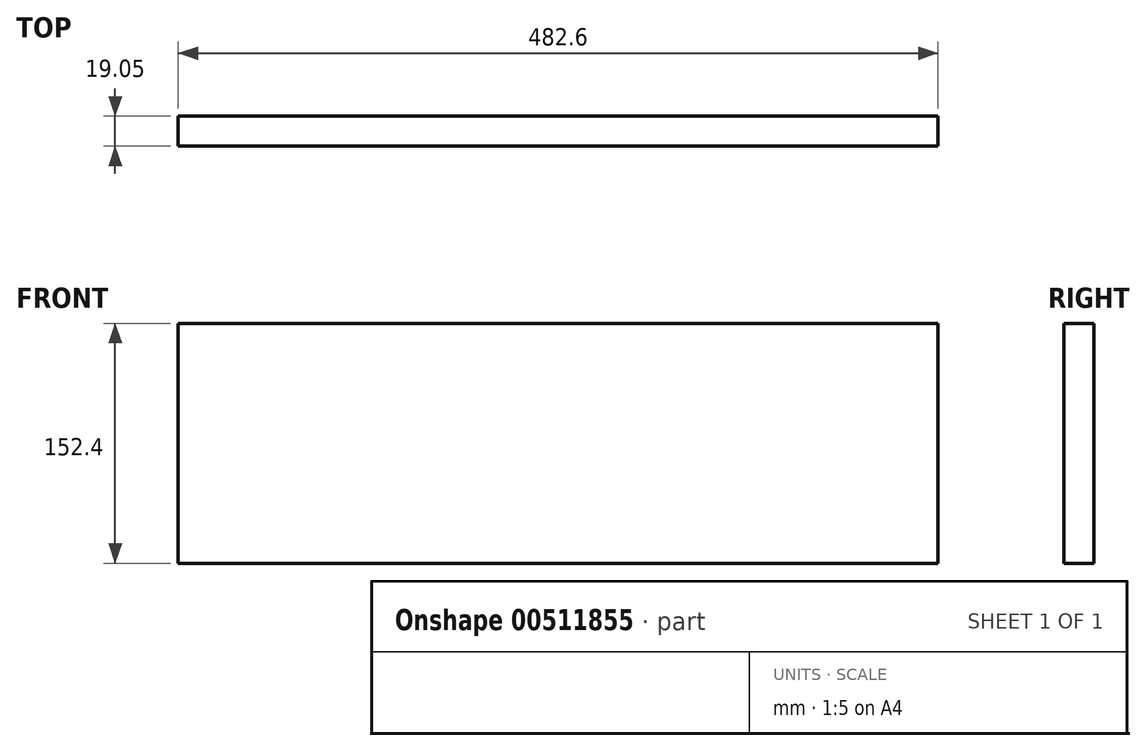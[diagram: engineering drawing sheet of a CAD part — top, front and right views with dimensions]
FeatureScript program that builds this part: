
annotation { "Feature Type Name" : "Feature", "Feature Type Description" : "" }
export const myFeature = defineFeature(function(context is Context, id is Id, definition is map)
    precondition{}
    {
        {
            var Q0;
            Q0=qCreatedBy(makeId("Front.planeOp"),FACE);
            var sketch = newSketch(context, id + "F0", { "sketchPlane" : qUnion([Q0])});
            skLineSegment(sketch, "E0.bottom", {"start": v(-156.37, 79.82) * mm, "end": v(326.23, 79.82) * mm});
            skLineSegment(sketch, "E0.top", {"start": v(-156.37, -72.58) * mm, "end": v(326.23, -72.58) * mm});
            skLineSegment(sketch, "E0.left", {"start": v(-156.37, 79.82) * mm, "end": v(-156.37, -72.58) * mm});
            skLineSegment(sketch, "E0.right", {"start": v(326.23, 79.82) * mm, "end": v(326.23, -72.58) * mm});
            skSolve(sketch);
        }
        {
            var Q0;
            Q0=makeQuery(id+"F0.imprint","IMPRINT",FACE,{"disambiguationData":[TD([[makeQuery(id+"F0.imprint","IMPRINT",EDGE,{"derivedFrom":sQuery(id+"F0.wireOp",EDGE,"E0.bottom")}),-1.0]])]});
            extrude(context, id + "F1", {"entities" : qUnion([Q0]), "depth" : 19.05 * mm});
        }
    });
